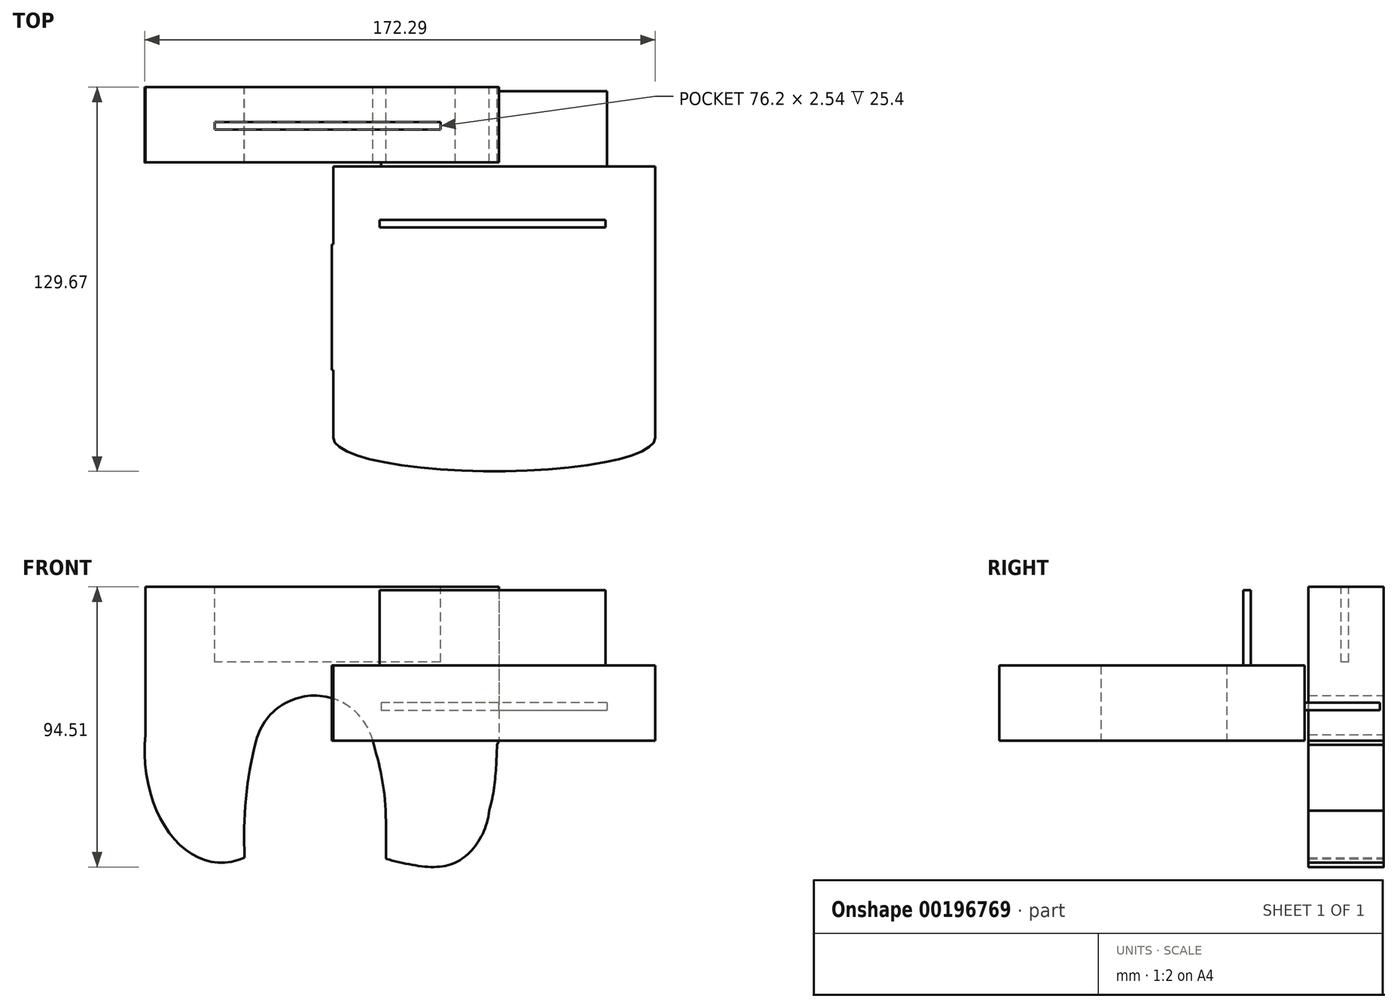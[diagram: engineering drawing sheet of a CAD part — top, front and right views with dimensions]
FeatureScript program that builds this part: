
annotation { "Feature Type Name" : "Feature", "Feature Type Description" : "" }
export const myFeature = defineFeature(function(context is Context, id is Id, definition is map)
    precondition{}
    {
        {
            var Q0;
            Q0=qCreatedBy(makeId("Front.planeOp"),FACE);
            var sketch = newSketch(context, id + "F0", { "sketchPlane" : qUnion([Q0])});
            skLineSegment(sketch, "E0.bottom", {"start": v(-57.05, 51.9) * mm, "end": v(62.24, 51.9) * mm});
            skLineSegment(sketch, "E0.left", {"start": v(-57.05, 51.9) * mm, "end": v(-57.05, 0) * mm});
            skLineSegment(sketch, "E0.right", {"start": v(62.24, 51.9) * mm, "end": v(62.24, 0) * mm});
            skEllipticalArc(sketch, "E1", {});
            skArc(sketch, "E2", {"start": v(-19.65, 0) * mm, "mid": v(0, 15.22) * mm, "end": v(19.65, 0) * mm});
            skArc(sketch, "E3", {"start": v(-19.65, 0) * mm, "mid": v(-23.15, -19.8) * mm, "end": v(-23.53, -39.9) * mm});
            skPoint(sketch, "E4.positionSnap0", {"position": v(-23.15, -19.8) * mm});
            skFitSpline(sketch, "E5", {"points": [v(19.65, 0) * mm, v(22.33, -10.42) * mm, v(23.86, -21.67) * mm, v(24.12, -39.9) * mm], "startDerivative": vector(9.7, -34.83) * mm, "endDerivative": vector(-0.33, -49.52) * mm});
            skEllipticalArc(sketch, "E6", {});
            skFitSpline(sketch, "E7", {"points": [v(61.58, -1.45) * mm, v(59, -23.63) * mm, v(47.48, -41.11) * mm, v(24.12, -39.9) * mm], "startDerivative": vector(-1.95, -65.96) * mm, "endDerivative": vector(-75.4, 18.75) * mm});
            skLineSegment(sketch, "E8", {"start": v(62.24, 0) * mm, "end": v(61.58, -1.45) * mm});
            const initialGuessF0  = {"E1": [-0.031359970569610596, -0.0033038801047950983, 0, 1, 0.037898974725976586, 0.025950012850302052, 1.4290915848100418, 3.447138165664776], "E6": [0.04174930974841118, -0.0196220800280571, 0, -1, 0.022740397602319717, 0.01751967887190923, 0.33303517252984977, 1.3936926101945368]};
            skSetInitialGuess(sketch, initialGuessF0);
            skSolve(sketch);
        }
        {
            var Q0;
            Q0 = qSketchRegion(id + "F0", true);
            extrude(context, id + "F1", {"entities" : qUnion([Q0]), "depth" : 25.4 * mm});
        }
        {
            var Q0;
            Q0=makeQuery(id+"F1.opExtrude","SWEPT_FACE",FACE,{"disambiguationData":[OSD([sQuery(id+"F0.wireOp",EDGE,"E0.bottom")])]});
            var sketch = newSketch(context, id + "F2", { "sketchPlane" : qUnion([Q0])});
            skLineSegment(sketch, "E9.bottom", {"start": v(42.54, -11.8) * mm, "end": v(-33.66, -11.8) * mm});
            skLineSegment(sketch, "E9.top", {"start": v(42.54, -14.34) * mm, "end": v(-33.66, -14.34) * mm});
            skLineSegment(sketch, "E9.left", {"start": v(42.54, -11.8) * mm, "end": v(42.54, -14.34) * mm});
            skLineSegment(sketch, "E9.right", {"start": v(-33.66, -11.8) * mm, "end": v(-33.66, -14.34) * mm});
            skPoint(sketch, "E9.middle", {"position": v(4.44, -13.07) * mm});
            skSolve(sketch);
        }
        {
            var Q0;
            Q0 = qSketchRegion(id + "F2", true);
            extrude(context, id + "F3", {"entities" : qUnion([Q0]), "operationType" : NewBodyOperationType.REMOVE, "oppositeDirection" : true, "depth" : 25.4 * mm});
        }
        {
            var Q0;
            Q0=qCreatedBy(makeId("Top.planeOp"),FACE);
            var sketch = newSketch(context, id + "F4", { "sketchPlane" : qUnion([Q0])});
            skEllipticalArc(sketch, "E10", {});
            skLineSegment(sketch, "E11.top", {"start": v(6.42, -118.71) * mm, "end": v(6.45, -118.71) * mm});
            skLineSegment(sketch, "E11.left", {"start": v(6.42, -95.44) * mm, "end": v(6.42, -118.71) * mm});
            skLineSegment(sketch, "E11.right", {"start": v(114.98, -95.44) * mm, "end": v(114.98, -118.71) * mm});
            skPoint(sketch, "E11.middle", {"position": v(60.7, -107.08) * mm});
            skLineSegment(sketch, "E12.bottom", {"start": v(6.42, -95.44) * mm, "end": v(5.82, -95.44) * mm});
            skLineSegment(sketch, "E12.top", {"start": v(6.39, -53.02) * mm, "end": v(5.82, -53.02) * mm});
            skLineSegment(sketch, "E12.left", {"start": v(114.98, -95.44) * mm, "end": v(114.98, -53.02) * mm});
            skLineSegment(sketch, "E12.right", {"start": v(5.82, -95.44) * mm, "end": v(5.82, -53.02) * mm});
            skLineSegment(sketch, "E13.top", {"start": v(114.98, -26.7) * mm, "end": v(6.39, -26.7) * mm});
            skLineSegment(sketch, "E13.left", {"start": v(114.98, -53.02) * mm, "end": v(114.98, -26.7) * mm});
            skLineSegment(sketch, "E13.right", {"start": v(6.39, -53.02) * mm, "end": v(6.39, -26.7) * mm});
            skLineSegment(sketch, "E14.trimOffspring", {"start": v(114.96, -118.71) * mm, "end": v(114.98, -118.71) * mm});
            skLineSegment(sketch, "E15.left", {"start": v(98.8, -35.43) * mm, "end": v(98.8, -32.9) * mm});
            skLineSegment(sketch, "E15.right", {"start": v(22.6, -35.43) * mm, "end": v(22.6, -32.9) * mm});
            skPoint(sketch, "E15.middle", {"position": v(60.7, -34.16) * mm});
            const initialGuessF4  = {"E10": [0.060704243185606806, -0.1183726499873712, 1, 0, 0.05428020568007042, 0.011295617237309806, 3.141592653589793, 0]};
            skSetInitialGuess(sketch, initialGuessF4);
            skSolve(sketch);
        }
        {
            var Q0;
            {var subQ5=sQuery(id+"F4.wireOp",EDGE,"E12.bottom");Q0=makeQuery(id+"F4.imprint","IMPRINT",FACE,{"disambiguationData":[TD([[makeQuery(id+"F4.imprint","IMPRINT",EDGE,{"derivedFrom":subQ5}),-1.0]])]});}
            extrude(context, id + "F5", {"entities" : qUnion([Q0]), "depth" : 25.4 * mm});
        }
        {
            var Q0;
            Q0=makeQuery(id+"F5.opExtrude","CAP_FACE",FACE,{"disambiguationData":[OSD([sQuery(id+"F4.wireOp",EDGE,"E10"),sQuery(id+"F4.wireOp",EDGE,"E11.left"),sQuery(id+"F4.wireOp",EDGE,"E11.right"),sQuery(id+"F4.wireOp",EDGE,"E12.bottom"),sQuery(id+"F4.wireOp",EDGE,"E12.top"),sQuery(id+"F4.wireOp",EDGE,"E12.left"),sQuery(id+"F4.wireOp",EDGE,"E12.right"),sQuery(id+"F4.wireOp",EDGE,"E13.top"),sQuery(id+"F4.wireOp",EDGE,"E13.left"),sQuery(id+"F4.wireOp",EDGE,"E13.right")])],"isStart":false});
            var sketch = newSketch(context, id + "F6", { "sketchPlane" : qUnion([Q0])});
            skLineSegment(sketch, "E16", {"start": v(22.01, -44.84) * mm, "end": v(98.21, -44.84) * mm});
            skLineSegment(sketch, "E17", {"start": v(22.01, -44.84) * mm, "end": v(22.01, -47.38) * mm});
            skLineSegment(sketch, "E18", {"start": v(22.01, -47.38) * mm, "end": v(98.21, -47.38) * mm});
            skLineSegment(sketch, "E19", {"start": v(98.21, -47.38) * mm, "end": v(98.21, -44.84) * mm});
            skSolve(sketch);
        }
        {
            var Q0;
            Q0 = qSketchRegion(id + "F6", true);
            extrude(context, id + "F7", {"entities" : qUnion([Q0]), "operationType" : NewBodyOperationType.ADD, "depth" : 25.4 * mm});
        }
        {
            var Q0;
            Q0=makeQuery(id+"F5.opExtrude","SWEPT_FACE",FACE,{"disambiguationData":[OSD([sQuery(id+"F4.wireOp",EDGE,"E13.top")])]});
            var sketch = newSketch(context, id + "F8", { "sketchPlane" : qUnion([Q0])});
            skLineSegment(sketch, "E20", {"start": v(-98.67, 12.89) * mm, "end": v(-22.47, 12.89) * mm});
            skLineSegment(sketch, "E21", {"start": v(-98.67, 12.89) * mm, "end": v(-98.67, 10.35) * mm});
            skLineSegment(sketch, "E22", {"start": v(-22.47, 12.89) * mm, "end": v(-22.47, 10.35) * mm});
            skLineSegment(sketch, "E23", {"start": v(-22.47, 10.35) * mm, "end": v(-98.67, 10.35) * mm});
            skSolve(sketch);
        }
        {
            var Q0;
            Q0 = qSketchRegion(id + "F8", true);
            extrude(context, id + "F9", {"entities" : qUnion([Q0]), "operationType" : NewBodyOperationType.ADD, "depth" : 25.4 * mm});
        }
    });
